# Revit family: Lighting_Fixture-Focal_Point-ID+3.5in-Downlight-Round-FLCS3_RO-Adjustable-Flood NEW
name_source: partatom
category: Lighting Fixtures
revit_build: Autodesk Revit Architecture 2014 (Build: 20140709_2115(x64)
units: mm (PartAtom-declared; Revit-internal decimal feet)

## types (1)
- Not a Type -  Load Type Catalog
    Apparent Load = 120 VA
    Color Filter = 16777215
    Color Temperature Comment = 2700K, 80+ CRI
    Default Elevation = 0' - 0"
    Description = ID+ 3.5in Round
    Diffuser Color = Plastic - Focal Point - Warm Diffuse
    Dimming Lamp Color Temperature Shift = <None>
    Distribution Note = Flood
    Driver = Please Load Accompanying Type Catalog (.txt)
    Driver Comment = Please Load Accompanying Type Catalog (.txt)
    Factory Options = For additional factory options see the Product Documentation Link
    Factory Options Comment = For additional factory options see the Product Documentation Link
    Flange Finish = Metal - Focal Point - Matte White Housing
    Frame Finish = Metal - Focal Point - Steel Galvanized
    Frequency = 60 Hz
    Housing Series = ID+ 3.5in Round
    IC Rated Height = 0' - 3 133/256"
    Installation and Service URL = http://www.focalpointlights.com
    Lamp = LED
    Light Source = 0' - 1"
    Manufacturer = Focal Point
    Manufacturer Fax Number = 773-247-8484
    Model = Please Load Accompanying Type Catalog (.txt)
    Number Of Lamps = 1
    Number of Poles = 1
    Optic = Adjustable Accent
    Phase = 1
    Photometric Web File = generic.ies
    Power Factor = 1
    Product Documentation Link = http://www.focalpointlights.com
    Product Name = ID+ 3.5in Round
    Product Page URL = http://www.focalpointlights.com
    Reflector Finish = Metal - Focal Point - Aluminum Raw
    Reflector Width = 0' - 3 1/2"
    Tilt Angle = 90.00°
    Trim Type = Round Overlap
    URL = http://www.focalpointlights.com
    Version = 2014-v1.0a
    Voltage = 120 V
    Wattage Comments = Please Load Accompanying Type Catalog (.txt)

## geometry (parser evidence)
native form markers: Blend x121, Sweep x7
no freeform markers — native parametric forms only
